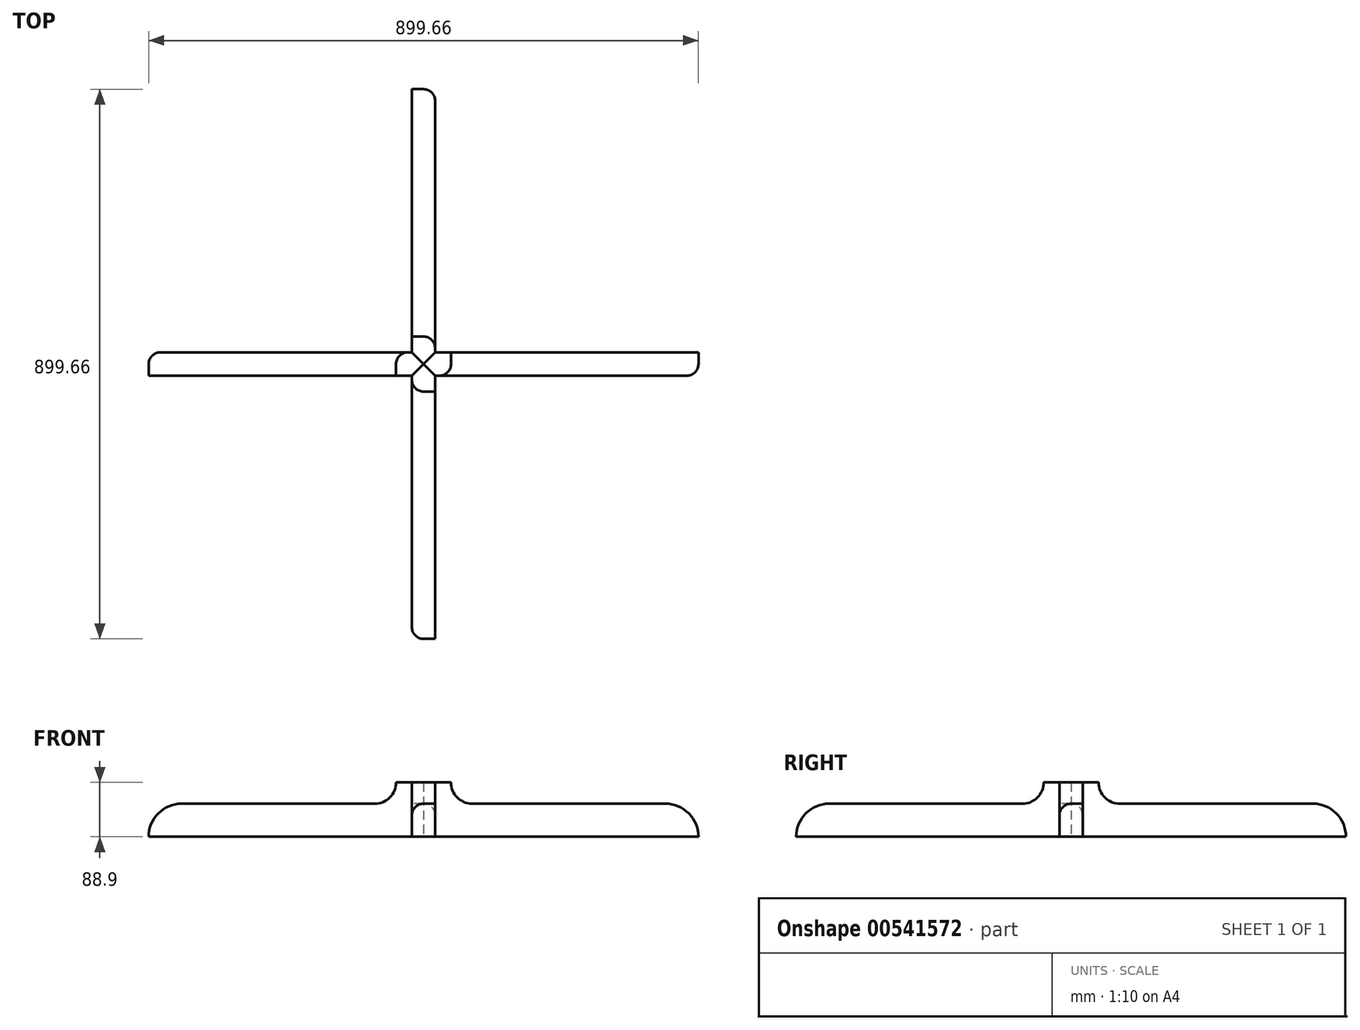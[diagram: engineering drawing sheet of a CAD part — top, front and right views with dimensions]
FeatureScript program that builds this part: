
annotation { "Feature Type Name" : "Feature", "Feature Type Description" : "" }
export const myFeature = defineFeature(function(context is Context, id is Id, definition is map)
    precondition{}
    {
        {
            var Q0;
            Q0=qCreatedBy(makeId("Front.planeOp"),FACE);
            var sketch = newSketch(context, id + "F0", { "sketchPlane" : qUnion([Q0])});
            skLineSegment(sketch, "E0.bottom", {"start": v(-19.05, 44.45) * mm, "end": v(19.05, 44.45) * mm});
            skLineSegment(sketch, "E0.top", {"start": v(-19.05, -44.45) * mm, "end": v(19.05, -44.45) * mm});
            skLineSegment(sketch, "E0.left", {"start": v(-19.05, 44.45) * mm, "end": v(-19.05, -44.45) * mm});
            skLineSegment(sketch, "E0.right", {"start": v(19.05, 44.45) * mm, "end": v(19.05, -44.45) * mm});
            skLineSegment(sketch, "E1", {"start": v(-19.05, 44.45) * mm, "end": v(19.05, -44.45) * mm, "construction": true});
            skSolve(sketch);
        }
        {
            var Q0;
            Q0 = qSketchRegion(id + "F0", true);
            extrude(context, id + "F1", {"entities" : qUnion([Q0]), "depth" : 449.83 * mm, "offsetDistance" : 25.4 * mm});
        }
        {
            var Q0;
            Q0=makeQuery(id+"F1.opExtrude","SWEPT_FACE",FACE,{"disambiguationData":[OSD([sQuery(id+"F0.wireOp",EDGE,"E0.right")])]});
            var sketch = newSketch(context, id + "F2", { "sketchPlane" : qUnion([Q0])});
            skLineSegment(sketch, "E2", {"start": v(-449.83, 9.7) * mm, "end": v(0, 9.7) * mm});
            skCircle(sketch, "E3", {"center": v(-79.7, 44.45) * mm, "radius": 34.74 * mm});
            skCircle(sketch, "E4", {"center": v(-395.68, -44.45) * mm, "radius": 54.16 * mm});
            skSolve(sketch);
        }
        {
            var Q0;
            {var subQ0=sQuery(id+"F2.wireOp",EDGE,"E2");var subQ1=sQuery(id+"F0.wireOp",EDGE,"E0.right");var subQ2=makeQuery(id+"F1.opExtrude","CAP_EDGE",EDGE,{"disambiguationData":[OSD([subQ1])],"isStart":false});var subQ3=makeQuery(id+"F2.imprint","INTERSECT",VERTEX,{"derivedFrom":[subQ2,subQ0]});Q0=makeQuery(id+"F2.imprint","IMPRINT",FACE,{"disambiguationData":[TD([[makeQuery(id+"F2.imprint","IMPRINT",EDGE,{"disambiguationData":[TD([[subQ3,-1.0]])],"derivedFrom":subQ0}),-1.0]])]});}
            var Q1;
            {var subQ1=sQuery(id+"F2.wireOp",EDGE,"E2");var subQ3=sQuery(id+"F0.wireOp",EDGE,"E0.right");var subQ7=makeQuery(id+"F1.opExtrude","CAP_EDGE",EDGE,{"disambiguationData":[OSD([subQ3])],"isStart":false});var subQ9=makeQuery(id+"F2.imprint","INTERSECT",VERTEX,{"derivedFrom":[subQ7,subQ1]});Q1=makeQuery(id+"F2.imprint","IMPRINT",FACE,{"disambiguationData":[TD([[makeQuery(id+"F2.imprint","IMPRINT",EDGE,{"disambiguationData":[TD([[subQ9,-1.0]])],"derivedFrom":subQ1}),1.0]])]});}
            var Q2;
            {var subQ0=sQuery(id+"F2.wireOp",EDGE,"E3");var subQ1=makeQuery(id+"F2.imprint","INTERSECT",VERTEX,{"derivedFrom":[sQuery(id+"F2.wireOp",EDGE,"E2"),subQ0]});Q2=makeQuery(id+"F2.imprint","IMPRINT",FACE,{"disambiguationData":[TD([[makeQuery(id+"F2.imprint","IMPRINT",EDGE,{"disambiguationData":[TD([[subQ1,1.0]])],"derivedFrom":subQ0}),1.0]])]});}
            extrude(context, id + "F3", {"entities" : qUnion([Q0, Q1, Q2]), "operationType" : NewBodyOperationType.REMOVE, "endBound" : BoundingType.THROUGH_ALL, "oppositeDirection" : true, "depth" : 25.4 * mm, "offsetDistance" : 25.4 * mm});
        }
        {
            var Q0;
            Q0=makeQuery(id+"F3.boolean.opBoolean","COPY",EDGE,{"derivedFrom":makeQuery(id+"F3.opExtrude","CAP_EDGE",EDGE,{"disambiguationData":[OSD([sQuery(id+"F2.wireOp",EDGE,"E4")])],"isStart":true})});
            var Q1;
            Q1=makeQuery(id+"F3.boolean.opBoolean","INTERSECT",EDGE,{"derivedFrom":[makeQuery(id+"F1.opExtrude","SWEPT_FACE",FACE,{"disambiguationData":[OSD([sQuery(id+"F0.wireOp",EDGE,"E0.left")])]}),makeQuery(id+"F3.opExtrude","SWEPT_FACE",FACE,{"disambiguationData":[OSD([sQuery(id+"F2.wireOp",EDGE,"E4")])]})]});
            var Q2;
            Q2=makeQuery(id+"F3.boolean.opBoolean","INTERSECT",EDGE,{"derivedFrom":[makeQuery(id+"F1.opExtrude","SWEPT_FACE",FACE,{"disambiguationData":[OSD([sQuery(id+"F0.wireOp",EDGE,"E0.left")])]}),makeQuery(id+"F3.opExtrude","SWEPT_FACE",FACE,{"disambiguationData":[OSD([sQuery(id+"F2.wireOp",EDGE,"E2")])]})]});
            var Q3;
            Q3=makeQuery(id+"F3.boolean.opBoolean","COPY",EDGE,{"derivedFrom":makeQuery(id+"F3.opExtrude","CAP_EDGE",EDGE,{"disambiguationData":[OSD([sQuery(id+"F2.wireOp",EDGE,"E2")])],"isStart":true})});
            var Q4;
            Q4=makeQuery(id+"F3.boolean.opBoolean","COPY",EDGE,{"derivedFrom":makeQuery(id+"F3.opExtrude","CAP_EDGE",EDGE,{"disambiguationData":[OSD([sQuery(id+"F2.wireOp",EDGE,"E3")])],"isStart":true})});
            var Q5;
            Q5=makeQuery(id+"F3.boolean.opBoolean","INTERSECT",EDGE,{"derivedFrom":[makeQuery(id+"F1.opExtrude","SWEPT_FACE",FACE,{"disambiguationData":[OSD([sQuery(id+"F0.wireOp",EDGE,"E0.left")])]}),makeQuery(id+"F3.opExtrude","SWEPT_FACE",FACE,{"disambiguationData":[OSD([sQuery(id+"F2.wireOp",EDGE,"E3")])]})]});
            fillet(context, id + "F4", {"entities" : qUnion([Q0, Q1, Q2, Q3, Q4, Q5]), "radius" : 19.05 * mm, "tangentPropagation" : true, "allowEdgeOverflow" : false});
        }
        {
            var Q0;
            Q0=makeQuery(id+"F1.opExtrude","CAP_EDGE",EDGE,{"disambiguationData":[OSD([sQuery(id+"F0.wireOp",EDGE,"E0.right")])],"isStart":true});
            var Q1;
            Q1=makeQuery(id+"F1.opExtrude","CAP_EDGE",EDGE,{"disambiguationData":[OSD([sQuery(id+"F0.wireOp",EDGE,"E0.left")])],"isStart":true});
            chamfer(context, id + "F5", {"entities" : qUnion([Q0, Q1]), "width" : 19.05 * mm, "tangentPropagation" : true});
        }
        {
            var Q0;
            Q0=makeQuery(id+"F1.opExtrude","SWEPT_BODY",BODY,{"disambiguationData":[OSD([sQuery(id+"F0.wireOp",EDGE,"E0.bottom"),sQuery(id+"F0.wireOp",EDGE,"E0.top"),sQuery(id+"F0.wireOp",EDGE,"E0.left"),sQuery(id+"F0.wireOp",EDGE,"E0.right")])]});
            var Q1;
            Q1=makeQuery(id+"F5.opChamfer","BLEND_EDGE",EDGE,{"blendedFrom":[makeQuery(id+"F1.opExtrude","CAP_EDGE",EDGE,{"disambiguationData":[OSD([sQuery(id+"F0.wireOp",EDGE,"E0.left")])],"isStart":true}),makeQuery(id+"F1.opExtrude","CAP_EDGE",EDGE,{"disambiguationData":[OSD([sQuery(id+"F0.wireOp",EDGE,"E0.right")])],"isStart":true})],"blendedInto":[]});
            circularPattern(context, id + "F6", {"entities" : qUnion([Q0]), "axis" : qUnion([Q1]), "angle" : 360 * degree, "instanceCount" : 4, "equalSpace" : true});
        }
    });
